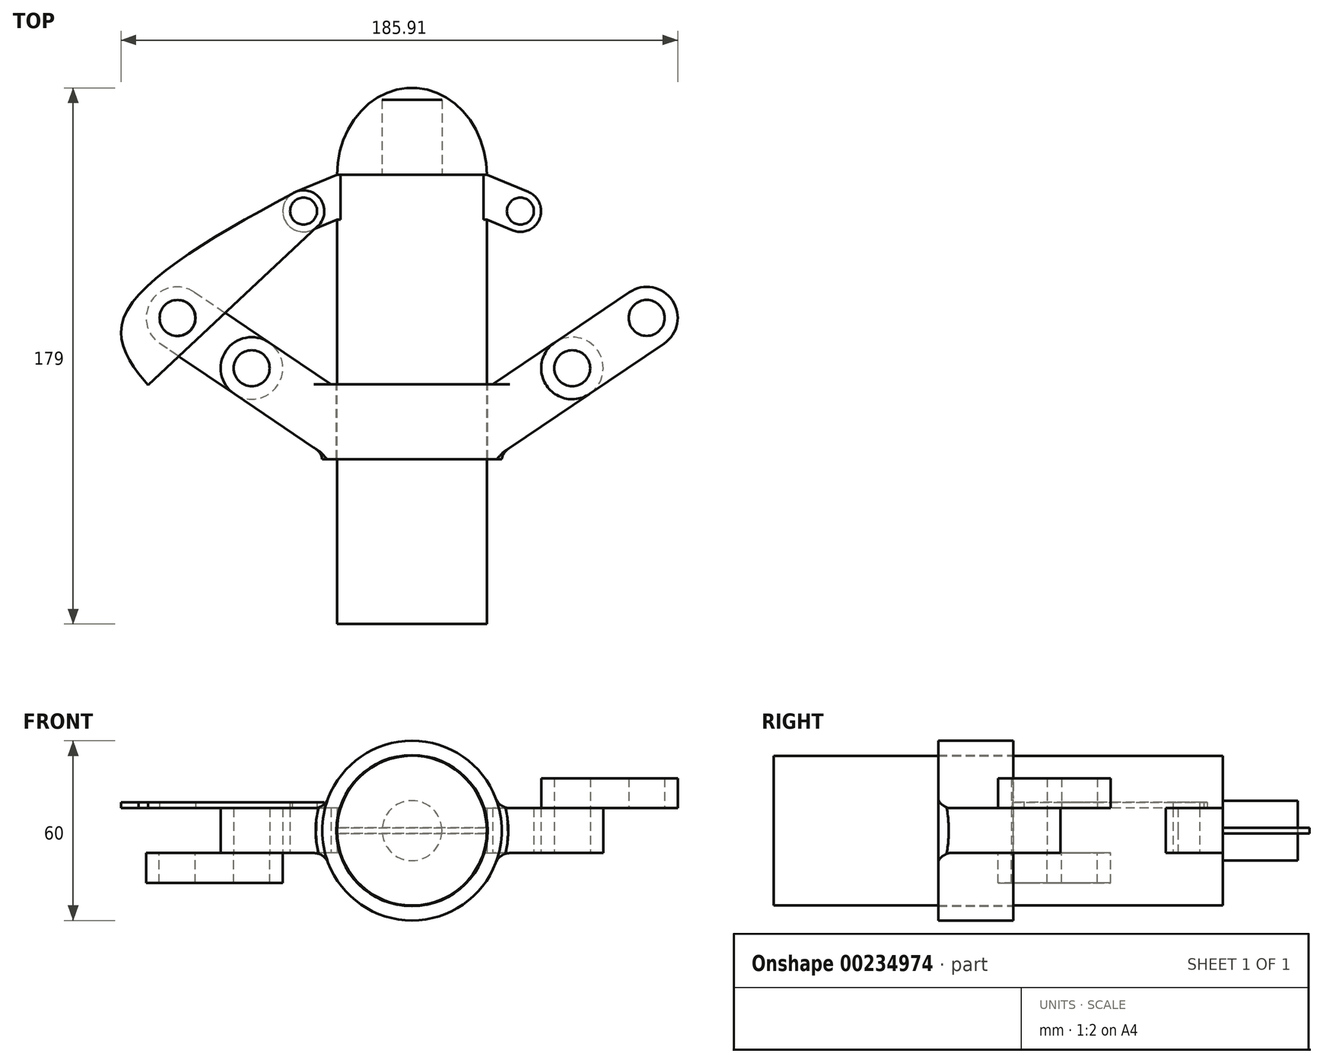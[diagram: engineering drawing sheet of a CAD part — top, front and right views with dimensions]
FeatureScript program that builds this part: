
annotation { "Feature Type Name" : "Feature", "Feature Type Description" : "" }
export const myFeature = defineFeature(function(context is Context, id is Id, definition is map)
    precondition{}
    {
        {
            var Q0;
            Q0=qCreatedBy(makeId("Front.planeOp"),FACE);
            var sketch = newSketch(context, id + "F0", { "sketchPlane" : qUnion([Q0])});
            skCircle(sketch, "E0", {"center": v(0, 0) * mm, "radius": 25 * mm});
            skSolve(sketch);
        }
        {
            var Q0;
            Q0 = qSketchRegion(id + "F0", true);
            extrude(context, id + "F1", {"entities" : qUnion([Q0]), "depth" : 150 * mm});
        }
        {
            var Q0;
            Q0=qCreatedBy(makeId("Front.planeOp"),FACE);
            cPlane(context, id + "F2", {"entities" : qUnion([Q0]), "cplaneType" : CPlaneType.OFFSET, "offset" : 70 * mm, "width" : 150 * mm, "height" : 150 * mm});
        }
        {
            var Q0;
            Q0=qCreatedBy(id+"F2.planeOp",FACE);
            var sketch = newSketch(context, id + "F3", { "sketchPlane" : qUnion([Q0])});
            skCircle(sketch, "E1", {"center": v(0, 0) * mm, "radius": 25.25 * mm});
            skCircle(sketch, "E2", {"center": v(0, 0) * mm, "radius": 30 * mm});
            skSolve(sketch);
        }
        {
            var Q0;
            Q0 = qSketchRegion(id + "F3", true);
            extrude(context, id + "F4", {"entities" : qUnion([Q0]), "depth" : 25 * mm});
        }
        {
            var Q0;
            Q0=qCreatedBy(makeId("Top.planeOp"),FACE);
            var sketch = newSketch(context, id + "F5", { "sketchPlane" : qUnion([Q0])});
            skLineSegment(sketch, "E3", {"start": v(0, 0) * mm, "end": v(0, -82.5) * mm});
            skLineSegment(sketch, "E4", {"start": v(0, -82.5) * mm, "end": v(27, -82.5) * mm});
            skLineSegment(sketch, "E5", {"start": v(27, -82.5) * mm, "end": v(27, -70) * mm});
            skLineSegment(sketch, "E6", {"start": v(27, -82.5) * mm, "end": v(27, -95) * mm});
            skLineSegment(sketch, "E7", {"start": v(27, -70) * mm, "end": v(47.72, -56.01) * mm});
            skLineSegment(sketch, "E8", {"start": v(27, -95) * mm, "end": v(59.31, -73.19) * mm});
            skArc(sketch, "E9", {"start": v(59.31, -73.19) * mm, "mid": v(62.1, -58.8) * mm, "end": v(47.72, -56.01) * mm});
            skLineSegment(sketch, "E10.MirrorCS", {"start": v(-27, -70) * mm, "end": v(-47.72, -56.01) * mm});
            skArc(sketch, "E11.MirrorC", {"start": v(-59.31, -73.19) * mm, "mid": v(-62.1, -58.8) * mm, "end": v(-47.72, -56.01) * mm});
            skLineSegment(sketch, "E12.MirrorCS", {"start": v(-27, -95) * mm, "end": v(-59.31, -73.19) * mm});
            skLineSegment(sketch, "E13.MirrorCS", {"start": v(-27, -82.5) * mm, "end": v(-27, -95) * mm});
            skLineSegment(sketch, "E14.MirrorCS", {"start": v(-27, -82.5) * mm, "end": v(-27, -70) * mm});
            skLineSegment(sketch, "E15.MirrorCS", {"start": v(0, -82.5) * mm, "end": v(-27, -82.5) * mm});
            skPoint(sketch, "E16.orphan", {"position": v(-47.72, -56.01) * mm});
            skPoint(sketch, "E17.MirrorCS.end.orphan", {"position": v(-59.31, -73.19) * mm});
            skCircle(sketch, "E18", {"center": v(53.52, -64.6) * mm, "radius": 6 * mm});
            skCircle(sketch, "E19", {"center": v(-53.52, -64.6) * mm, "radius": 6 * mm});
            skSolve(sketch);
        }
        {
            var Q0;
            Q0 = qSketchRegion(id + "F5", true);
            extrude(context, id + "F6", {"entities" : qUnion([Q0]), "operationType" : NewBodyOperationType.ADD, "endBound" : BoundingType.SYMMETRIC, "depth" : 15 * mm});
        }
        {
            var Q0;
            Q0=makeQuery(id+"F6.boolean.opBoolean","INTERSECT",EDGE,{"derivedFrom":[makeQuery(id+"F4.opExtrude","SWEPT_FACE",FACE,{"disambiguationData":[OSD([sQuery(id+"F3.wireOp",EDGE,"E2")])]}),makeQuery(id+"F6.opExtrude","CAP_FACE",FACE,{"disambiguationData":[OSD([sQuery(id+"F5.wireOp",EDGE,"E5"),sQuery(id+"F5.wireOp",EDGE,"E6"),sQuery(id+"F5.wireOp",EDGE,"E7"),sQuery(id+"F5.wireOp",EDGE,"E8"),sQuery(id+"F5.wireOp",EDGE,"E9"),sQuery(id+"F5.wireOp",EDGE,"E18")])],"isStart":true})]});
            var Q1;
            Q1=makeQuery(id+"F6.boolean.opBoolean","INTERSECT",EDGE,{"derivedFrom":[makeQuery(id+"F4.opExtrude","SWEPT_FACE",FACE,{"disambiguationData":[OSD([sQuery(id+"F3.wireOp",EDGE,"E2")])]}),makeQuery(id+"F6.opExtrude","SWEPT_FACE",FACE,{"disambiguationData":[OSD([sQuery(id+"F5.wireOp",EDGE,"E8")])]})]});
            var Q2;
            Q2=makeQuery(id+"F6.boolean.opBoolean","INTERSECT",EDGE,{"derivedFrom":[makeQuery(id+"F4.opExtrude","SWEPT_FACE",FACE,{"disambiguationData":[OSD([sQuery(id+"F3.wireOp",EDGE,"E2")])]}),makeQuery(id+"F6.opExtrude","CAP_FACE",FACE,{"disambiguationData":[OSD([sQuery(id+"F5.wireOp",EDGE,"E10.MirrorCS"),sQuery(id+"F5.wireOp",EDGE,"E11.MirrorC"),sQuery(id+"F5.wireOp",EDGE,"E12.MirrorCS"),sQuery(id+"F5.wireOp",EDGE,"E13.MirrorCS"),sQuery(id+"F5.wireOp",EDGE,"E14.MirrorCS"),sQuery(id+"F5.wireOp",EDGE,"E19")])],"isStart":true})]});
            var Q3;
            Q3=makeQuery(id+"F6.boolean.opBoolean","INTERSECT",EDGE,{"derivedFrom":[makeQuery(id+"F4.opExtrude","SWEPT_FACE",FACE,{"disambiguationData":[OSD([sQuery(id+"F3.wireOp",EDGE,"E2")])]}),makeQuery(id+"F6.opExtrude","SWEPT_FACE",FACE,{"disambiguationData":[OSD([sQuery(id+"F5.wireOp",EDGE,"E12.MirrorCS")])]})]});
            var Q4;
            Q4=makeQuery(id+"F6.boolean.opBoolean","INTERSECT",EDGE,{"derivedFrom":[makeQuery(id+"F4.opExtrude","SWEPT_FACE",FACE,{"disambiguationData":[OSD([sQuery(id+"F3.wireOp",EDGE,"E2")])]}),makeQuery(id+"F6.opExtrude","CAP_FACE",FACE,{"disambiguationData":[OSD([sQuery(id+"F5.wireOp",EDGE,"E10.MirrorCS"),sQuery(id+"F5.wireOp",EDGE,"E11.MirrorC"),sQuery(id+"F5.wireOp",EDGE,"E12.MirrorCS"),sQuery(id+"F5.wireOp",EDGE,"E13.MirrorCS"),sQuery(id+"F5.wireOp",EDGE,"E14.MirrorCS"),sQuery(id+"F5.wireOp",EDGE,"E19")])],"isStart":false})]});
            var Q5;
            Q5=makeQuery(id+"F6.boolean.opBoolean","INTERSECT",EDGE,{"derivedFrom":[makeQuery(id+"F4.opExtrude","SWEPT_FACE",FACE,{"disambiguationData":[OSD([sQuery(id+"F3.wireOp",EDGE,"E2")])]}),makeQuery(id+"F6.opExtrude","CAP_FACE",FACE,{"disambiguationData":[OSD([sQuery(id+"F5.wireOp",EDGE,"E5"),sQuery(id+"F5.wireOp",EDGE,"E6"),sQuery(id+"F5.wireOp",EDGE,"E7"),sQuery(id+"F5.wireOp",EDGE,"E8"),sQuery(id+"F5.wireOp",EDGE,"E9"),sQuery(id+"F5.wireOp",EDGE,"E18")])],"isStart":false})]});
            var Q6;
            Q6=makeQuery(id+"F6.opExtrude","SWEPT_EDGE",EDGE,{"disambiguationData":[OSD([sQuery(id+"F5.wireOp",EDGE,"E5"),sQuery(id+"F5.wireOp",EDGE,"E7")])]});
            var Q7;
            Q7=makeQuery(id+"F6.opExtrude","SWEPT_EDGE",EDGE,{"disambiguationData":[OSD([sQuery(id+"F5.wireOp",EDGE,"E10.MirrorCS"),sQuery(id+"F5.wireOp",EDGE,"E14.MirrorCS")])]});
            fillet(context, id + "F7", {"entities" : qUnion([Q0, Q1, Q2, Q3, Q4, Q5, Q6, Q7]), "radius" : 5 * mm, "tangentPropagation" : true, "allowEdgeOverflow" : false});
        }
        {
            var Q0;
            Q0=qCreatedBy(makeId("Top.planeOp"),FACE);
            var sketch = newSketch(context, id + "F8", { "sketchPlane" : qUnion([Q0])});
            skLineSegment(sketch, "E20", {"start": v(0, 0) * mm, "end": v(-25, 0) * mm});
            skLineSegment(sketch, "E21", {"start": v(0, 0) * mm, "end": v(25, 0) * mm});
            skLineSegment(sketch, "E22", {"start": v(-25, 0) * mm, "end": v(-25, -15) * mm});
            skLineSegment(sketch, "E23", {"start": v(-25, 0) * mm, "end": v(-38.85, -5.75) * mm});
            skLineSegment(sketch, "E24", {"start": v(-25, -15) * mm, "end": v(-33.54, -18.55) * mm});
            skArc(sketch, "E25", {"start": v(-38.85, -5.75) * mm, "mid": v(-42.6, -14.8) * mm, "end": v(-33.54, -18.55) * mm});
            skLineSegment(sketch, "E26.MirrorCS", {"start": v(25, 0) * mm, "end": v(38.85, -5.75) * mm});
            skLineSegment(sketch, "E27.MirrorCS", {"start": v(25, 0) * mm, "end": v(25, -15) * mm});
            skLineSegment(sketch, "E28.MirrorCS", {"start": v(25, -15) * mm, "end": v(33.54, -18.55) * mm});
            skArc(sketch, "E29.MirrorCS", {"start": v(38.85, -5.75) * mm, "mid": v(42.6, -14.8) * mm, "end": v(33.54, -18.55) * mm});
            skCircle(sketch, "E30", {"center": v(-36.2, -12.15) * mm, "radius": 4.5 * mm});
            skCircle(sketch, "E31", {"center": v(36.2, -12.15) * mm, "radius": 4.5 * mm});
            skLineSegment(sketch, "E32", {"start": v(-25, 0) * mm, "end": v(-23, 0) * mm});
            skLineSegment(sketch, "E33", {"start": v(-23, 0) * mm, "end": v(-23, -15) * mm});
            skLineSegment(sketch, "E34", {"start": v(-23, -15) * mm, "end": v(-25, -15) * mm});
            skLineSegment(sketch, "E35", {"start": v(25, 0) * mm, "end": v(23, 0) * mm});
            skLineSegment(sketch, "E36", {"start": v(23, 0) * mm, "end": v(23, -15) * mm});
            skLineSegment(sketch, "E37", {"start": v(23, -15) * mm, "end": v(25, -15) * mm});
            skSolve(sketch);
        }
        {
            var Q0;
            Q0 = qSketchRegion(id + "F8", true);
            extrude(context, id + "F9", {"entities" : qUnion([Q0]), "operationType" : NewBodyOperationType.ADD, "endBound" : BoundingType.SYMMETRIC, "depth" : 15 * mm});
        }
        {
            var Q0;
            Q0=makeQuery(id+"F6.opExtrude","CAP_FACE",FACE,{"disambiguationData":[OSD([sQuery(id+"F5.wireOp",EDGE,"E10.MirrorCS"),sQuery(id+"F5.wireOp",EDGE,"E11.MirrorC"),sQuery(id+"F5.wireOp",EDGE,"E12.MirrorCS"),sQuery(id+"F5.wireOp",EDGE,"E13.MirrorCS"),sQuery(id+"F5.wireOp",EDGE,"E14.MirrorCS"),sQuery(id+"F5.wireOp",EDGE,"E19")])],"isStart":true});
            var sketch = newSketch(context, id + "F10", { "sketchPlane" : qUnion([Q0])});
            skCircle(sketch, "E38", {"center": v(-53.52, 64.6) * mm, "radius": 6 * mm});
            skArc(sketch, "E39", {"start": v(-47.72, 56.01) * mm, "mid": v(-44.93, 70.4) * mm, "end": v(-59.31, 73.19) * mm});
            skLineSegment(sketch, "E40", {"start": v(-59.31, 73.19) * mm, "end": v(-84.18, 56.4) * mm});
            skLineSegment(sketch, "E41", {"start": v(-72.59, 39.23) * mm, "end": v(-47.72, 56.01) * mm});
            skArc(sketch, "E42", {"start": v(-84.18, 56.4) * mm, "mid": v(-86.97, 42.02) * mm, "end": v(-72.59, 39.23) * mm});
            skCircle(sketch, "E43", {"center": v(-78.38, 47.81) * mm, "radius": 6 * mm});
            skSolve(sketch);
        }
        {
            var Q0;
            Q0 = qSketchRegion(id + "F10", true);
            extrude(context, id + "F11", {"entities" : qUnion([Q0]), "depth" : 10 * mm});
        }
        {
            var Q0;
            Q0=makeQuery(id+"F6.opExtrude","CAP_FACE",FACE,{"disambiguationData":[OSD([sQuery(id+"F5.wireOp",EDGE,"E5"),sQuery(id+"F5.wireOp",EDGE,"E6"),sQuery(id+"F5.wireOp",EDGE,"E7"),sQuery(id+"F5.wireOp",EDGE,"E8"),sQuery(id+"F5.wireOp",EDGE,"E9"),sQuery(id+"F5.wireOp",EDGE,"E18")])],"isStart":false});
            var sketch = newSketch(context, id + "F12", { "sketchPlane" : qUnion([Q0])});
            skCircle(sketch, "E44", {"center": v(53.52, -64.6) * mm, "radius": 6 * mm});
            skArc(sketch, "E45", {"start": v(47.78, -55.97) * mm, "mid": v(44.93, -70.4) * mm, "end": v(59.37, -73.15) * mm});
            skLineSegment(sketch, "E46", {"start": v(47.72, -56.01) * mm, "end": v(72.59, -39.23) * mm});
            skLineSegment(sketch, "E47", {"start": v(59.31, -73.19) * mm, "end": v(84.18, -56.4) * mm});
            skArc(sketch, "E48", {"start": v(84.18, -56.4) * mm, "mid": v(86.97, -42.02) * mm, "end": v(72.59, -39.23) * mm});
            skCircle(sketch, "E49", {"center": v(78.38, -47.81) * mm, "radius": 6 * mm});
            skSolve(sketch);
        }
        {
            var Q0;
            Q0 = qSketchRegion(id + "F12", true);
            extrude(context, id + "F13", {"entities" : qUnion([Q0]), "depth" : 10 * mm});
        }
        {
            var Q0;
            Q0=makeQuery(id+"F9.opExtrude","CAP_FACE",FACE,{"disambiguationData":[OSD([sQuery(id+"F8.wireOp",EDGE,"E23"),sQuery(id+"F8.wireOp",EDGE,"E24"),sQuery(id+"F8.wireOp",EDGE,"E25"),sQuery(id+"F8.wireOp",EDGE,"E30"),sQuery(id+"F8.wireOp",EDGE,"E32"),sQuery(id+"F8.wireOp",EDGE,"E33"),sQuery(id+"F8.wireOp",EDGE,"E34")])],"isStart":false});
            var sketch = newSketch(context, id + "F14", { "sketchPlane" : qUnion([Q0])});
            skCircle(sketch, "E50", {"center": v(-36.2, -12.15) * mm, "radius": 4.5 * mm});
            skCircle(sketch, "E51", {"center": v(-78.28, -47.83) * mm, "radius": 6 * mm});
            skArc(sketch, "E52", {"start": v(-33.54, -18.55) * mm, "mid": v(-30.08, -8.9) * mm, "end": v(-40.01, -6.37) * mm});
            skFitSpline(sketch, "E53", {"points": [v(-38.85, -5.75) * mm, v(-96.28, -47.83) * mm, v(-91.3, -66.4) * mm], "startDerivative": vector(-126.85, -67.29) * mm, "endDerivative": vector(39.38, -52.46) * mm});
            skLineSegment(sketch, "E54", {"start": v(-91.3, -66.4) * mm, "end": v(-88.1, -70.25) * mm});
            skLineSegment(sketch, "E55", {"start": v(-88.1, -70.25) * mm, "end": v(-31.46, -17.2) * mm});
            skSolve(sketch);
        }
        {
            var Q0;
            Q0 = qSketchRegion(id + "F14", true);
            extrude(context, id + "F15", {"entities" : qUnion([Q0]), "depth" : 2 * mm});
        }
        {
            var Q0;
            Q0=makeQuery(id+"F9.boolean.opBoolean","MERGE",FACE,{"derivedFrom":[makeQuery(id+"F1.opExtrude","CAP_FACE",FACE,{"disambiguationData":[OSD([sQuery(id+"F0.wireOp",EDGE,"E0")])],"isStart":true}),makeQuery(id+"F9.opExtrude","SWEPT_FACE",FACE,{"disambiguationData":[OSD([sQuery(id+"F8.wireOp",EDGE,"E32")])]}),makeQuery(id+"F9.opExtrude","SWEPT_FACE",FACE,{"disambiguationData":[OSD([sQuery(id+"F8.wireOp",EDGE,"E35")])]})]});
            var sketch = newSketch(context, id + "F16", { "sketchPlane" : qUnion([Q0])});
            skCircle(sketch, "E56", {"center": v(0, 0) * mm, "radius": 10 * mm});
            skSolve(sketch);
        }
        {
            var Q0;
            Q0 = qSketchRegion(id + "F16", true);
            extrude(context, id + "F17", {"entities" : qUnion([Q0]), "depth" : 25 * mm});
        }
        {
            var Q0;
            Q0=qCreatedBy(makeId("Top.planeOp"),FACE);
            var sketch = newSketch(context, id + "F18", { "sketchPlane" : qUnion([Q0])});
            skEllipticalArc(sketch, "E57", {});
            skLineSegment(sketch, "E58", {"start": v(-25, 0) * mm, "end": v(25, 0) * mm});
            const initialGuessF18  = {"E57": [0, 0, 0, 1, 0.029, 0.025, 4.71238898038469, 1.5707963267948966]};
            skSetInitialGuess(sketch, initialGuessF18);
            skSolve(sketch);
        }
        {
            var Q0;
            Q0 = qSketchRegion(id + "F18", true);
            extrude(context, id + "F19", {"entities" : qUnion([Q0]), "endBound" : BoundingType.SYMMETRIC, "depth" : 2 * mm});
        }
    });
